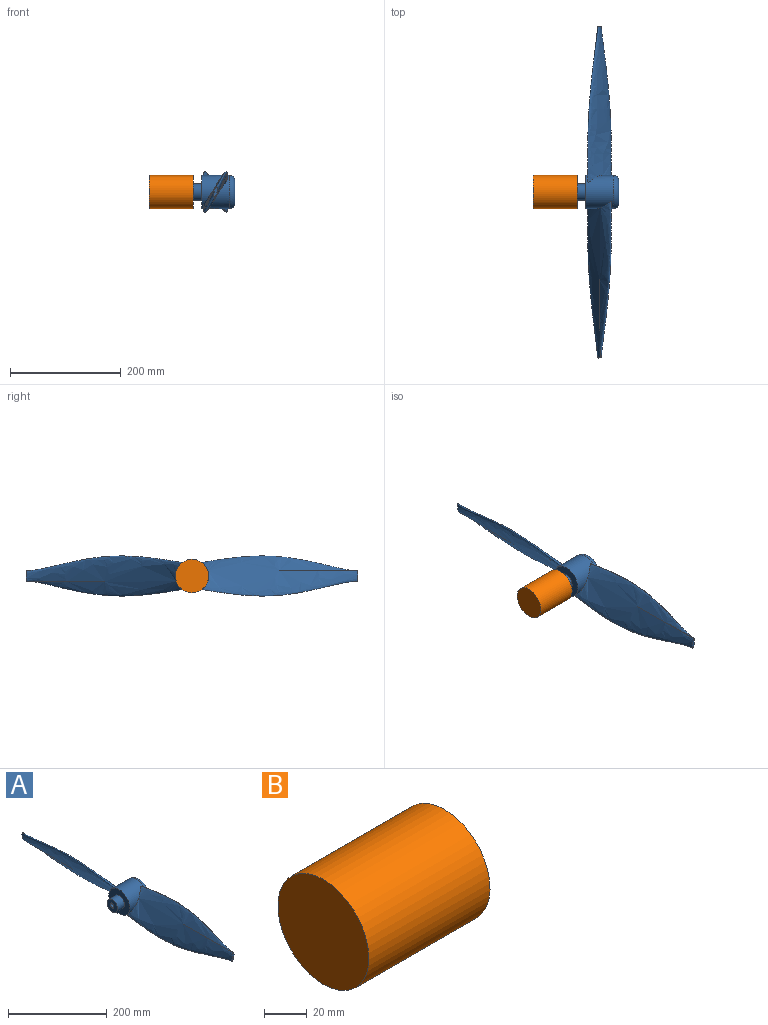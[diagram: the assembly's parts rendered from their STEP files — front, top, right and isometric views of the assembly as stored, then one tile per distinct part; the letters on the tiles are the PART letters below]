
ASSEMBLY  parts=2 mates=1
PART A: 15 faces, bbox 80x600x72.4 mm
  f0: plane 30x30mm, normal (-1,0,0), area 624.5mm2, adj f4,f10,f11,f12,f13
  f1: plane 40x40mm, normal (1,0,0), area 1256.6mm2, adj f9
  f2: cylinder r=30mm len=60mm, axis (1,0,0), area 8453.5mm2, adj f3,f5,f7,f9
  f3: plane 60x60mm, normal (-1,0,0), area 2120.6mm2, adj f2,f4
  f4: cylinder r=15mm len=30mm, axis (1,0,0), area 1885mm2, adj f0,f3
  f5: bspline ~282.58x72.34mm, area 35680.6mm2, adj f2,f6
  f6: plane 19.79x6.12mm, normal (0,1,0), area 78.6mm2, adj f5
  f7: bspline ~282.58x72.34mm, area 35680.6mm2, adj f2,f8
  f8: plane 19.79x6.12mm, normal (0,-1,0), area 78.6mm2, adj f7
  f9: torus R=20mm, axis (-1,0,0), area 2602.2mm2, adj f1,f2
  f10: plane 20x2mm, normal (0,0,-1), area 40mm2, adj f0,f11,f13,f14
  f11: plane 20x2mm, normal (0,-1,0), area 40mm2, adj f0,f10,f12,f14
  f12: cylinder r=5mm len=20mm, axis (-1,0,0), area 588mm2, adj f0,f11,f13,f14
  f13: plane 20x2mm, normal (0,1,0), area 40mm2, adj f0,f10,f12,f14
  f14: plane 11.9x10mm, normal (-1,0,0), area 82.4mm2, adj f10,f11,f12,f13
PART B: 5 faces, bbox 95x60x60 mm
  f0: plane 60x60mm, normal (-1,0,0), area 2827.4mm2, adj f4
  f1: plane 10x10mm, normal (1,0,0), area 78.5mm2, adj f2
  f2: cylinder r=5mm len=15mm, axis (-1,0,0), area 471.2mm2, adj f1,f3
  f3: plane 60x60mm, normal (1,0,0), area 2748.9mm2, adj f2,f4
  f4: cylinder r=30mm len=80mm, axis (-1,0,0), area 15079.6mm2, adj f0,f3
PLACE A rot(axis=(1,0,0),180deg) t=(-97.29,29.56,26.14)mm
PLACE B t=(-217.29,29.56,26.14)mm
MATE revolute A.f2 <-> B.f2  axis (-1,0,0) through (-122.29,29.56,26.14)mm
